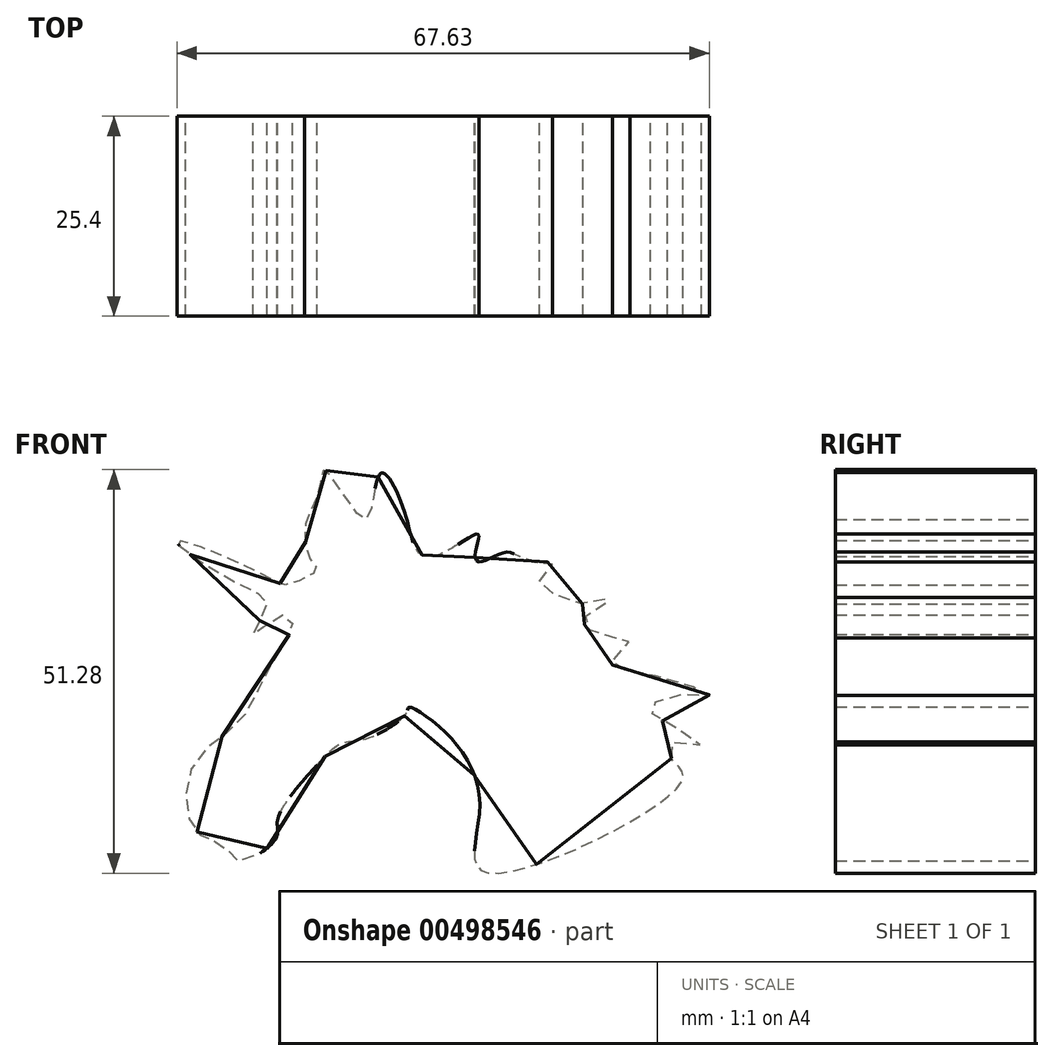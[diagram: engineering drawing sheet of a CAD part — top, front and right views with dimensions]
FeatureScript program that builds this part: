
annotation { "Feature Type Name" : "Feature", "Feature Type Description" : "" }
export const myFeature = defineFeature(function(context is Context, id is Id, definition is map)
    precondition{}
    {
        {
            var Q0;
            Q0=qCreatedBy(makeId("Front.planeOp"),FACE);
            var sketch = newSketch(context, id + "F0", { "sketchPlane" : qUnion([Q0])});
            skFitSpline(sketch, "E0", {"points": [v(31.43, -10.84) * mm, v(31.43, -8.83) * mm, v(35.23, -9.04) * mm, v(29.28, -5.34) * mm, v(28.87, -4.32) * mm, v(31.43, -2.78) * mm, v(36.26, -2.78) * mm, v(31.43, -0.83) * mm, v(24.76, 0.6) * mm, v(23.94, 1.43) * mm, v(26.2, 4.3) * mm, v(23.33, 4.5) * mm, v(20.25, 6.56) * mm, v(21.69, 8) * mm, v(23.94, 9.64) * mm, v(21.28, 8.82) * mm, v(16.14, 10.26) * mm, v(14.7, 11.7) * mm, v(16.35, 13.95) * mm, v(13.27, 14.16) * mm, v(10.6, 15.39) * mm, v(7.11, 14.16) * mm, v(6.5, 15.18) * mm, v(6.9, 17.65) * mm, v(2.19, 15.18) * mm, v(-0.69, 15.39) * mm, v(-2.54, 20.72) * mm, v(-5.4, 25.45) * mm, v(-6.85, 20.31) * mm, v(-7.87, 19.7) * mm, v(-12.6, 25.86) * mm, v(-13.2, 23.6) * mm, v(-14.85, 19.5) * mm, v(-15.06, 16.82) * mm, v(-14.24, 14.16) * mm, v(-13.62, 13.13) * mm, v(-17.31, 11.28) * mm, v(-19.16, 11.9) * mm, v(-31.27, 16.82) * mm, v(-25.32, 12.3) * mm, v(-19.98, 9.23) * mm, v(-20.6, 7.18) * mm, v(-21.63, 4.92) * mm, v(-18.14, 7.38) * mm, v(-16.7, 6.36) * mm, v(-19.37, 1.22) * mm, v(-23.47, -6.17) * mm, v(-28.8, -10.84) * mm, v(-30.04, -17.66) * mm, v(-27.78, -20.94) * mm, v(-25.32, -21.97) * mm, v(-23.68, -23.82) * mm, v(-18.75, -20.94) * mm, v(-18.55, -18.48) * mm, v(-12.8, -10.84) * mm, v(-10.34, -8.83) * mm, v(-7.05, -8.22) * mm, v(-2.13, -4.93) * mm, v(-1.92, -4.32) * mm, v(2.19, -6.99) * mm, v(7.11, -16.84) * mm, v(7.73, -25.26) * mm, v(32.77, -13.76) * mm, v(31.43, -10.84) * mm]});
            skSolve(sketch);
        }
        {
            var Q0;
            Q0=sQuery(id+"F0.wireOp",EDGE,"E0");
            extrude(context, id + "F1", {"bodyType" : ToolBodyType.SURFACE, "surfaceEntities" : qUnion([Q0]), "depth" : 5.08 * mm});
        }
        {
            var Q0;
            Q0 = qSketchRegion(id + "F0", true);
            extrude(context, id + "F2", {"entities" : qUnion([Q0]), "depth" : 25.4 * mm});
        }
    });
